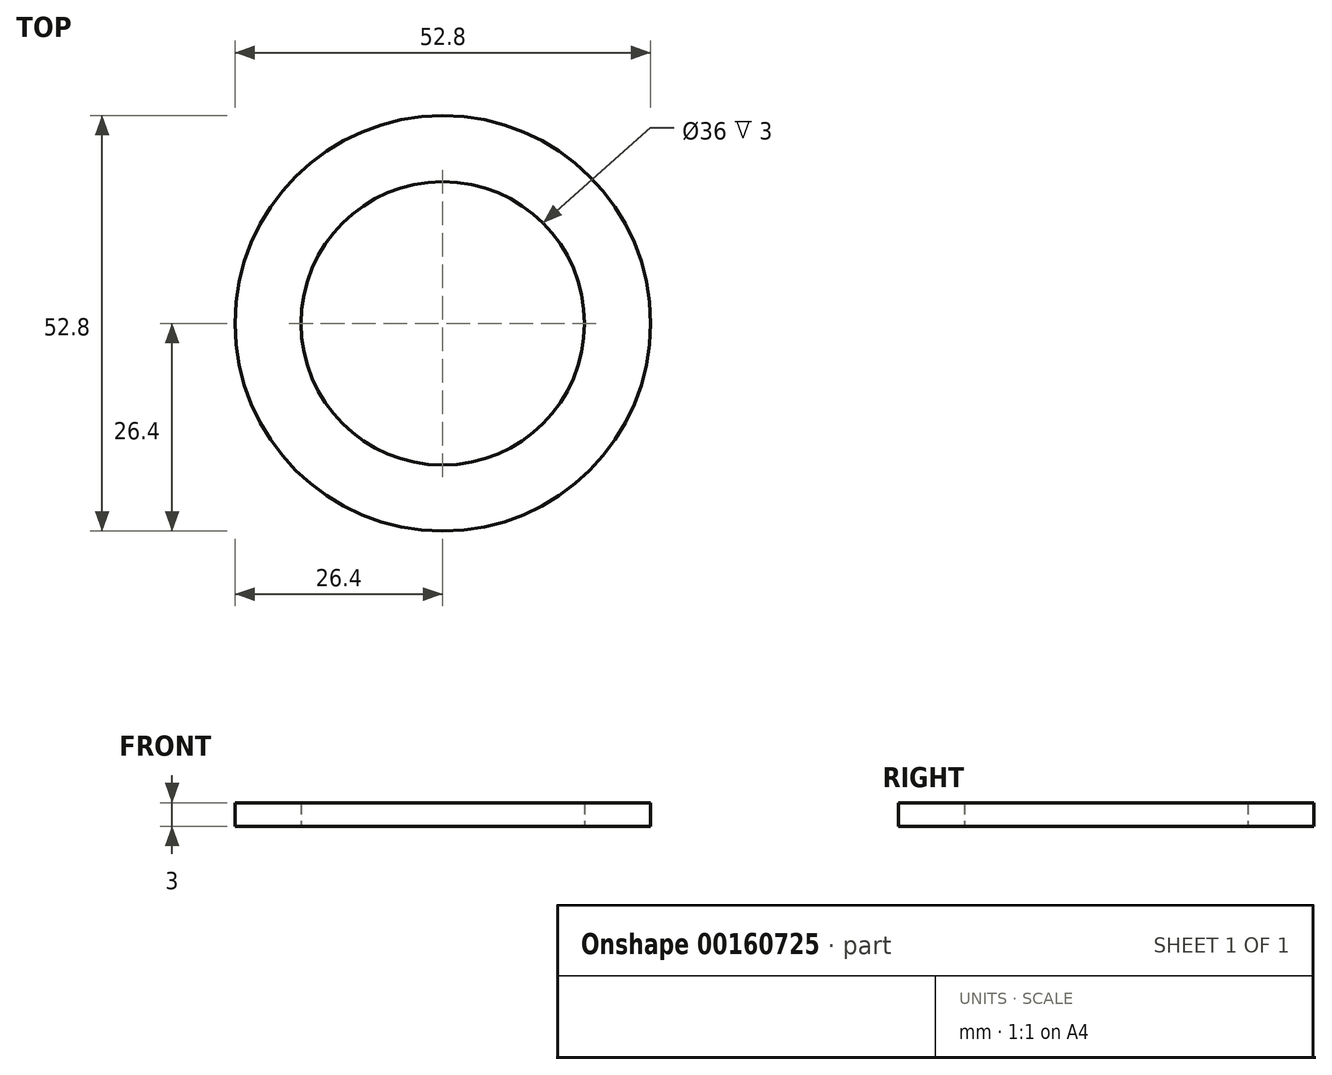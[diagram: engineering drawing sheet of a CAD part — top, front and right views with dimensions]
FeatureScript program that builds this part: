
annotation { "Feature Type Name" : "Feature", "Feature Type Description" : "" }
export const myFeature = defineFeature(function(context is Context, id is Id, definition is map)
    precondition{}
    {
        {
            var Q0;
            Q0=qCreatedBy(makeId("Top.planeOp"),FACE);
            var sketch = newSketch(context, id + "F0", { "sketchPlane" : qUnion([Q0])});
            skCircle(sketch, "E0", {"center": v(0, 0) * mm, "radius": 26.4 * mm});
            skCircle(sketch, "E1", {"center": v(0, 0) * mm, "radius": 18 * mm});
            skSolve(sketch);
        }
        {
            var Q0;
            Q0 = qSketchRegion(id + "F0", true);
            extrude(context, id + "F1", {"entities" : qUnion([Q0]), "depth" : 3 * mm});
        }
    });
